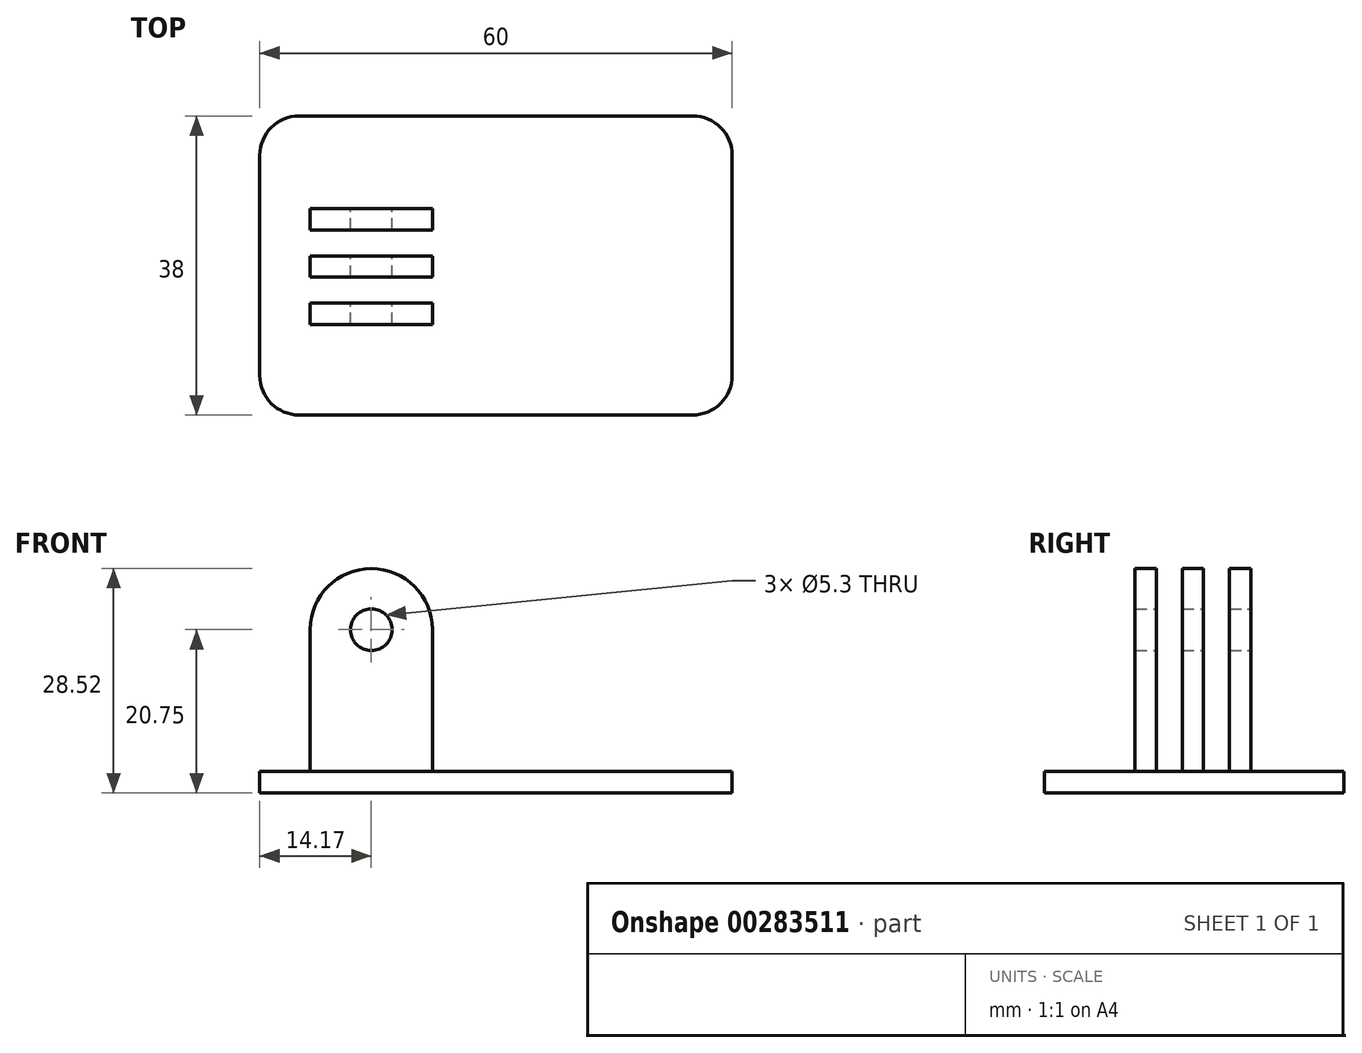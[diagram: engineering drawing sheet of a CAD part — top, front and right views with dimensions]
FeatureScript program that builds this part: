
annotation { "Feature Type Name" : "Feature", "Feature Type Description" : "" }
export const myFeature = defineFeature(function(context is Context, id is Id, definition is map)
    precondition{}
    {
        {
            var Q0;
            Q0=qCreatedBy(makeId("Top.planeOp"),FACE);
            var sketch = newSketch(context, id + "F0", { "sketchPlane" : qUnion([Q0])});
            skLineSegment(sketch, "E0.bottom", {"start": v(-1.42, -29.53) * mm, "end": v(48.58, -29.53) * mm});
            skLineSegment(sketch, "E0.top", {"start": v(-1.42, 8.47) * mm, "end": v(48.58, 8.47) * mm});
            skLineSegment(sketch, "E0.left", {"start": v(-6.42, -24.53) * mm, "end": v(-6.42, 3.47) * mm});
            skLineSegment(sketch, "E0.right", {"start": v(53.58, -24.53) * mm, "end": v(53.58, 3.47) * mm});
            skLineSegment(sketch, "E1.bottom", {"start": v(0, -18.02) * mm, "end": v(15.5, -18.02) * mm});
            skLineSegment(sketch, "E1.top", {"start": v(0, -15.32) * mm, "end": v(15.5, -15.32) * mm});
            skLineSegment(sketch, "E1.left", {"start": v(0, -18.02) * mm, "end": v(0, -15.32) * mm});
            skLineSegment(sketch, "E1.right", {"start": v(15.5, -18.02) * mm, "end": v(15.5, -15.32) * mm});
            skLineSegment(sketch, "E2.1.0.0", {"start": v(0, -12.02) * mm, "end": v(15.5, -12.02) * mm});
            skLineSegment(sketch, "E2.1.0.1", {"start": v(0, -9.32) * mm, "end": v(15.5, -9.32) * mm});
            skLineSegment(sketch, "E2.1.0.2", {"start": v(0, -12.02) * mm, "end": v(0, -9.32) * mm});
            skLineSegment(sketch, "E2.1.0.3", {"start": v(15.5, -12.02) * mm, "end": v(15.5, -9.32) * mm});
            skLineSegment(sketch, "E2.2.0.0", {"start": v(0, -6.02) * mm, "end": v(15.5, -6.02) * mm});
            skLineSegment(sketch, "E2.2.0.1", {"start": v(0, -3.32) * mm, "end": v(15.5, -3.32) * mm});
            skLineSegment(sketch, "E2.2.0.2", {"start": v(0, -6.02) * mm, "end": v(0, -3.32) * mm});
            skLineSegment(sketch, "E2.2.0.3", {"start": v(15.5, -6.02) * mm, "end": v(15.5, -3.32) * mm});
            skLineSegment(sketch, "E2.direction1", {"start": v(0, -18.02) * mm, "end": v(0, -12.02) * mm, "construction": true});
            skPoint(sketch, "E3.visualSharp", {"position": v(-6.42, 8.47) * mm});
            skArc(sketch, "E3.filletArc", {"start": v(-1.42, 8.47) * mm, "mid": v(-4.95, 7) * mm, "end": v(-6.42, 3.47) * mm});
            skPoint(sketch, "E4.visualSharp", {"position": v(53.58, -29.53) * mm});
            skArc(sketch, "E4.filletArc", {"start": v(48.58, -29.53) * mm, "mid": v(52.12, -28.07) * mm, "end": v(53.58, -24.53) * mm});
            skPoint(sketch, "E5.visualSharp", {"position": v(-6.42, -29.53) * mm});
            skArc(sketch, "E5.filletArc", {"start": v(-6.42, -24.53) * mm, "mid": v(-4.95, -28.07) * mm, "end": v(-1.42, -29.53) * mm});
            skPoint(sketch, "E6.visualSharp", {"position": v(53.58, 8.47) * mm});
            skArc(sketch, "E6.filletArc", {"start": v(53.58, 3.47) * mm, "mid": v(52.12, 7) * mm, "end": v(48.58, 8.47) * mm});
            skSolve(sketch);
        }
        {
            var Q0;
            Q0=makeQuery(id+"F0.imprint","IMPRINT",FACE,{"disambiguationData":[TD([[makeQuery(id+"F0.imprint","IMPRINT",EDGE,{"derivedFrom":sQuery(id+"F0.wireOp",EDGE,"E0.bottom")}),1.0]])]});
            extrude(context, id + "F1", {"entities" : qUnion([Q0]), "depth" : 2.75 * mm});
        }
        {
            var Q0;
            Q0=makeQuery(id+"F0.imprint","IMPRINT",FACE,{"disambiguationData":[TD([[makeQuery(id+"F0.imprint","IMPRINT",EDGE,{"derivedFrom":sQuery(id+"F0.wireOp",EDGE,"E1.bottom")}),1.0]])]});
            var Q1;
            Q1=makeQuery(id+"F0.imprint","IMPRINT",FACE,{"disambiguationData":[TD([[makeQuery(id+"F0.imprint","IMPRINT",EDGE,{"derivedFrom":sQuery(id+"F0.wireOp",EDGE,"E2.1.0.0")}),1.0]])]});
            var Q2;
            Q2=makeQuery(id+"F0.imprint","IMPRINT",FACE,{"disambiguationData":[TD([[makeQuery(id+"F0.imprint","IMPRINT",EDGE,{"derivedFrom":sQuery(id+"F0.wireOp",EDGE,"E2.2.0.0")}),1.0]])]});
            extrude(context, id + "F2", {"entities" : qUnion([Q0, Q1, Q2]), "operationType" : NewBodyOperationType.ADD, "depth" : 30 * mm});
        }
        {
            var Q0;
            Q0=makeQuery(id+"F2.opExtrude","SWEPT_FACE",FACE,{"disambiguationData":[OSD([sQuery(id+"F0.wireOp",EDGE,"E2.2.0.1")])]});
            var sketch = newSketch(context, id + "F3", { "sketchPlane" : qUnion([Q0])});
            skCircle(sketch, "E7", {"center": v(-7.75, 20.75) * mm, "radius": 2.65 * mm});
            skPoint(sketch, "E7.centerSnap0", {"position": v(-7.75, 30) * mm});
            skArc(sketch, "E8", {"start": v(0, 20.75) * mm, "mid": v(-7.75, 28.52) * mm, "end": v(-15.5, 20.75) * mm});
            skSolve(sketch);
        }
        {
            var Q0;
            {var subQ1=sQuery(id+"F0.wireOp",EDGE,"E2.2.0.1");var subQ6=makeQuery(id+"F2.opExtrude","CAP_EDGE",EDGE,{"disambiguationData":[OSD([subQ1])],"isStart":false});Q0=makeQuery(id+"F3.imprint","IMPRINT",FACE,{"disambiguationData":[TD([[makeQuery(id+"F3.imprint","IMPRINT",EDGE,{"derivedFrom":subQ6}),1.0]])]});}
            var Q1;
            Q1=makeQuery(id+"F3.imprint","IMPRINT",FACE,{"disambiguationData":[TD([[makeQuery(id+"F3.imprint","IMPRINT",EDGE,{"derivedFrom":sQuery(id+"F3.wireOp",EDGE,"E7")}),1.0]])]});
            extrude(context, id + "F4", {"entities" : qUnion([Q0, Q1]), "operationType" : NewBodyOperationType.REMOVE, "endBound" : BoundingType.THROUGH_ALL, "oppositeDirection" : true, "depth" : 25 * mm});
        }
        {
            var Q0;
            Q0=makeQuery(id+"F3.imprint","IMPRINT",FACE,{"disambiguationData":[TD([[makeQuery(id+"F3.imprint","IMPRINT",EDGE,{"derivedFrom":sQuery(id+"F3.wireOp",EDGE,"E7")}),1.0]])]});
            extrude(context, id + "F5", {"entities" : qUnion([Q0]), "operationType" : NewBodyOperationType.REMOVE, "endBound" : BoundingType.THROUGH_ALL, "oppositeDirection" : true, "depth" : 25 * mm});
        }
    });
